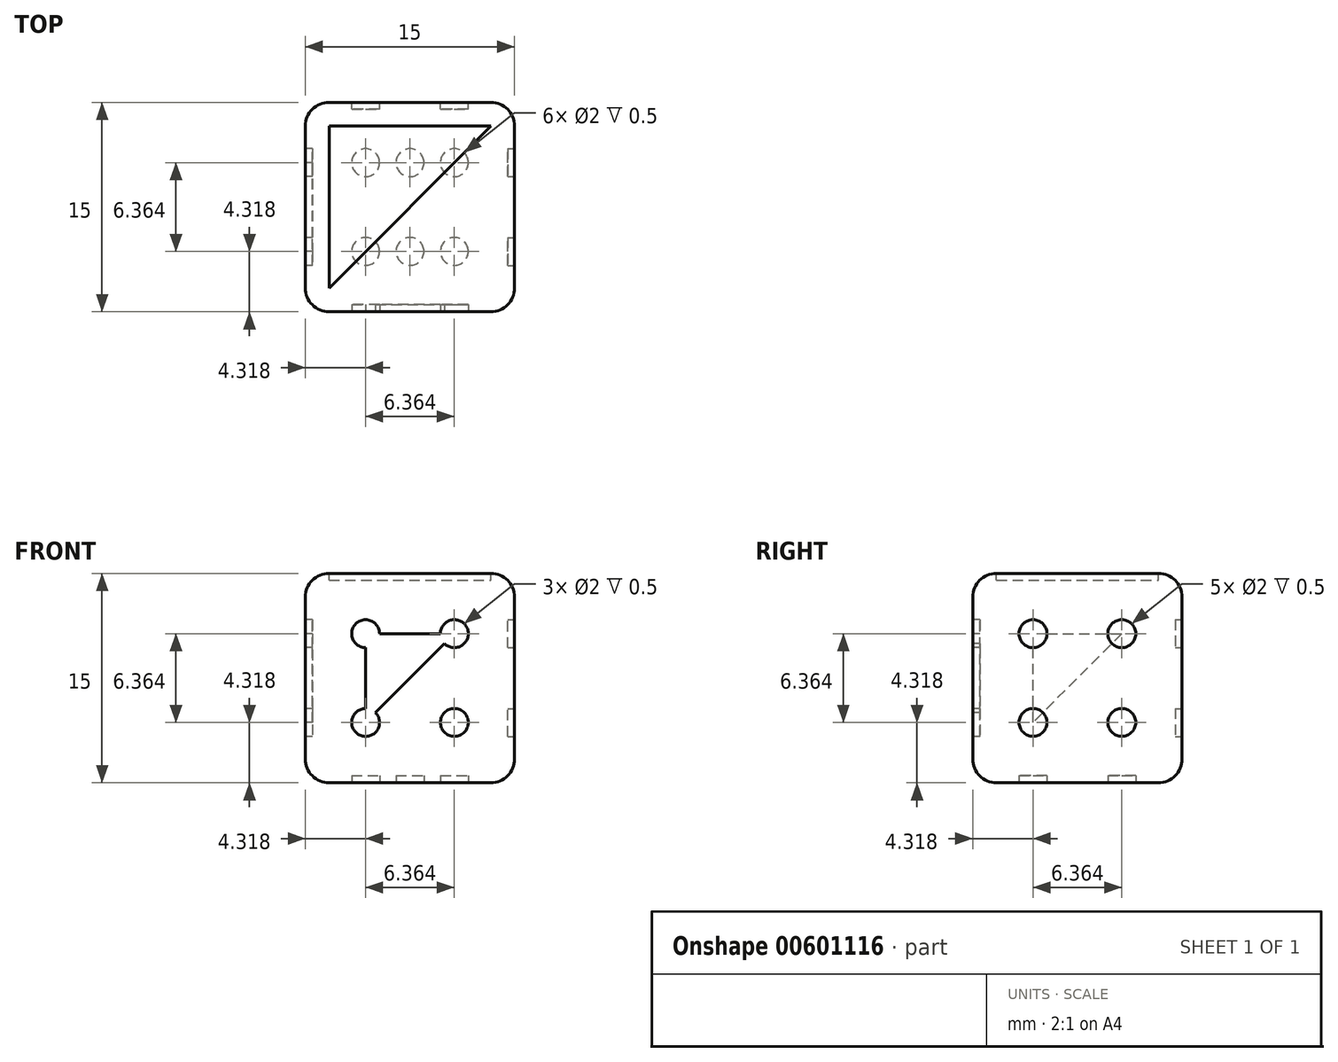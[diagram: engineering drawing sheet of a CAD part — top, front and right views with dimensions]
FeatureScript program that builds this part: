
annotation { "Feature Type Name" : "Feature", "Feature Type Description" : "" }
export const myFeature = defineFeature(function(context is Context, id is Id, definition is map)
    precondition{}
    {
        {
            var Q0;
            Q0=qCreatedBy(makeId("Front.planeOp"),FACE);
            var sketch = newSketch(context, id + "F0", { "sketchPlane" : qUnion([Q0])});
            skLineSegment(sketch, "E0.bottom", {"start": v(7.5, -7.5) * mm, "end": v(-7.5, -7.5) * mm});
            skLineSegment(sketch, "E0.top", {"start": v(7.5, 7.5) * mm, "end": v(-7.5, 7.5) * mm});
            skLineSegment(sketch, "E0.left", {"start": v(7.5, -7.5) * mm, "end": v(7.5, 7.5) * mm});
            skLineSegment(sketch, "E0.right", {"start": v(-7.5, -7.5) * mm, "end": v(-7.5, 7.5) * mm});
            skPoint(sketch, "E0.middle", {"position": v(0, 0) * mm});
            skSolve(sketch);
        }
        {
            var Q0;
            Q0 = qSketchRegion(id + "F0", true);
            extrude(context, id + "F1", {"entities" : qUnion([Q0]), "depth" : 15 * mm, "offsetDistance" : 25.4 * mm});
        }
        {
            var Q0;
            Q0=makeQuery(id+"F1.opExtrude","SWEPT_EDGE",EDGE,{"disambiguationData":[OSD([sQuery(id+"F0.wireOp",EDGE,"E0.bottom"),sQuery(id+"F0.wireOp",EDGE,"E0.right")])]});
            var Q1;
            Q1=makeQuery(id+"F1.opExtrude","CAP_EDGE",EDGE,{"disambiguationData":[OSD([sQuery(id+"F0.wireOp",EDGE,"E0.bottom")])],"isStart":true});
            var Q2;
            Q2=makeQuery(id+"F1.opExtrude","CAP_EDGE",EDGE,{"disambiguationData":[OSD([sQuery(id+"F0.wireOp",EDGE,"E0.right")])],"isStart":true});
            var Q3;
            Q3=makeQuery(id+"F1.opExtrude","CAP_EDGE",EDGE,{"disambiguationData":[OSD([sQuery(id+"F0.wireOp",EDGE,"E0.bottom")])],"isStart":false});
            var Q4;
            Q4=makeQuery(id+"F1.opExtrude","SWEPT_EDGE",EDGE,{"disambiguationData":[OSD([sQuery(id+"F0.wireOp",EDGE,"E0.bottom"),sQuery(id+"F0.wireOp",EDGE,"E0.left")])]});
            var Q5;
            Q5=makeQuery(id+"F1.opExtrude","CAP_EDGE",EDGE,{"disambiguationData":[OSD([sQuery(id+"F0.wireOp",EDGE,"E0.left")])],"isStart":false});
            var Q6;
            Q6=makeQuery(id+"F1.opExtrude","CAP_EDGE",EDGE,{"disambiguationData":[OSD([sQuery(id+"F0.wireOp",EDGE,"E0.right")])],"isStart":false});
            var Q7;
            Q7=makeQuery(id+"F1.opExtrude","SWEPT_FACE",FACE,{"disambiguationData":[OSD([sQuery(id+"F0.wireOp",EDGE,"E0.top")])]});
            var Q8;
            Q8=makeQuery(id+"F1.opExtrude","CAP_EDGE",EDGE,{"disambiguationData":[OSD([sQuery(id+"F0.wireOp",EDGE,"E0.left")])],"isStart":true});
            fillet(context, id + "F2", {"entities" : qUnion([Q0, Q1, Q2, Q3, Q4, Q5, Q6, Q7, Q8]), "radius" : 1.7 * mm, "tangentPropagation" : true, "allowEdgeOverflow" : false});
        }
        {
            var Q0;
            Q0=makeQuery(id+"F1.opExtrude","SWEPT_FACE",FACE,{"disambiguationData":[OSD([sQuery(id+"F0.wireOp",EDGE,"E0.top")])]});
            var sketch = newSketch(context, id + "F3", { "sketchPlane" : qUnion([Q0])});
            skLineSegment(sketch, "E1", {"start": v(5.8, -13.3) * mm, "end": v(-5.8, -1.7) * mm});
            skLineSegment(sketch, "E2", {"start": v(-5.8, -1.7) * mm, "end": v(-5.8, -13.3) * mm});
            skLineSegment(sketch, "E3", {"start": v(-5.8, -13.3) * mm, "end": v(5.8, -1.7) * mm});
            skCircle(sketch, "E4", {"center": v(0, -7.5) * mm, "radius": 1 * mm});
            skSolve(sketch);
        }
        {
            var Q0;
            Q0=makeQuery(id+"F1.opExtrude","SWEPT_FACE",FACE,{"disambiguationData":[OSD([sQuery(id+"F0.wireOp",EDGE,"E0.bottom")])]});
            var sketch = newSketch(context, id + "F4", { "sketchPlane" : qUnion([Q0])});
            skLineSegment(sketch, "E5", {"start": v(-5.8, 13.3) * mm, "end": v(-5.8, 1.7) * mm});
            skPoint(sketch, "E6.middle", {"position": v(0, 7.5) * mm});
            skCircle(sketch, "E7", {"center": v(-3.18, 4.32) * mm, "radius": 1 * mm});
            skCircle(sketch, "E8", {"center": v(0, 4.32) * mm, "radius": 1 * mm});
            skCircle(sketch, "E9", {"center": v(3.18, 4.32) * mm, "radius": 1 * mm});
            skCircle(sketch, "E10", {"center": v(3.18, 10.68) * mm, "radius": 1 * mm});
            skCircle(sketch, "E11", {"center": v(-3.18, 10.68) * mm, "radius": 1 * mm});
            skCircle(sketch, "E12", {"center": v(0, 10.68) * mm, "radius": 1 * mm});
            skSolve(sketch);
        }
        {
            var Q0;
            Q0=makeQuery(id+"F1.opExtrude","CAP_FACE",FACE,{"disambiguationData":[OSD([sQuery(id+"F0.wireOp",EDGE,"E0.bottom"),sQuery(id+"F0.wireOp",EDGE,"E0.top"),sQuery(id+"F0.wireOp",EDGE,"E0.left"),sQuery(id+"F0.wireOp",EDGE,"E0.right")])],"isStart":false});
            var sketch = newSketch(context, id + "F5", { "sketchPlane" : qUnion([Q0])});
            skLineSegment(sketch, "E13", {"start": v(5.8, -5.8) * mm, "end": v(-5.8, 5.8) * mm});
            skLineSegment(sketch, "E14", {"start": v(-5.8, 5.8) * mm, "end": v(-5.8, -5.8) * mm});
            skLineSegment(sketch, "E15", {"start": v(-5.8, -5.8) * mm, "end": v(5.8, 5.8) * mm});
            skLineSegment(sketch, "E16.bottom", {"start": v(3.18, 3.18) * mm, "end": v(-3.18, 3.18) * mm});
            skLineSegment(sketch, "E16.top", {"start": v(3.18, -3.18) * mm, "end": v(-3.18, -3.18) * mm});
            skLineSegment(sketch, "E16.left", {"start": v(3.18, 3.18) * mm, "end": v(3.18, -3.18) * mm});
            skLineSegment(sketch, "E16.right", {"start": v(-3.18, 3.18) * mm, "end": v(-3.18, -3.18) * mm});
            skPoint(sketch, "E16.middle", {"position": v(0, 0) * mm});
            skCircle(sketch, "E17", {"center": v(-3.18, -3.18) * mm, "radius": 1 * mm});
            skCircle(sketch, "E18", {"center": v(0, 0) * mm, "radius": 1 * mm});
            skCircle(sketch, "E19", {"center": v(-3.18, 3.18) * mm, "radius": 1 * mm});
            skCircle(sketch, "E20", {"center": v(3.18, 3.18) * mm, "radius": 1 * mm});
            skCircle(sketch, "E21", {"center": v(3.18, -3.18) * mm, "radius": 1 * mm});
            skSolve(sketch);
        }
        {
            var Q0;
            Q0=makeQuery(id+"F1.opExtrude","CAP_FACE",FACE,{"disambiguationData":[OSD([sQuery(id+"F0.wireOp",EDGE,"E0.bottom"),sQuery(id+"F0.wireOp",EDGE,"E0.top"),sQuery(id+"F0.wireOp",EDGE,"E0.left"),sQuery(id+"F0.wireOp",EDGE,"E0.right")])],"isStart":true});
            var sketch = newSketch(context, id + "F6", { "sketchPlane" : qUnion([Q0])});
            skLineSegment(sketch, "E22", {"start": v(-5.8, 5.8) * mm, "end": v(5.8, -5.8) * mm});
            skLineSegment(sketch, "E23", {"start": v(5.8, 5.8) * mm, "end": v(-5.8, -5.8) * mm});
            skLineSegment(sketch, "E24.bottom", {"start": v(-3.18, -3.18) * mm, "end": v(3.18, -3.18) * mm});
            skLineSegment(sketch, "E24.top", {"start": v(-3.18, 3.18) * mm, "end": v(3.18, 3.18) * mm});
            skLineSegment(sketch, "E24.left", {"start": v(-3.18, -3.18) * mm, "end": v(-3.18, 3.18) * mm});
            skLineSegment(sketch, "E24.right", {"start": v(3.18, -3.18) * mm, "end": v(3.18, 3.18) * mm});
            skPoint(sketch, "E24.middle", {"position": v(0, 0) * mm});
            skCircle(sketch, "E25", {"center": v(3.18, -3.18) * mm, "radius": 1 * mm});
            skCircle(sketch, "E26", {"center": v(-3.18, 3.18) * mm, "radius": 1 * mm});
            skSolve(sketch);
        }
        {
            var Q0;
            Q0=makeQuery(id+"F1.opExtrude","SWEPT_FACE",FACE,{"disambiguationData":[OSD([sQuery(id+"F0.wireOp",EDGE,"E0.right")])]});
            var sketch = newSketch(context, id + "F7", { "sketchPlane" : qUnion([Q0])});
            skLineSegment(sketch, "E27", {"start": v(1.7, -5.8) * mm, "end": v(13.3, 5.8) * mm});
            skLineSegment(sketch, "E28", {"start": v(13.3, 5.8) * mm, "end": v(1.7, 5.8) * mm});
            skLineSegment(sketch, "E29", {"start": v(1.7, 5.8) * mm, "end": v(13.3, -5.8) * mm});
            skLineSegment(sketch, "E30.bottom", {"start": v(10.68, -3.18) * mm, "end": v(4.32, -3.18) * mm});
            skLineSegment(sketch, "E30.top", {"start": v(10.68, 3.18) * mm, "end": v(4.32, 3.18) * mm});
            skLineSegment(sketch, "E30.left", {"start": v(10.68, -3.18) * mm, "end": v(10.68, 3.18) * mm});
            skLineSegment(sketch, "E30.right", {"start": v(4.32, -3.18) * mm, "end": v(4.32, 3.18) * mm});
            skPoint(sketch, "E30.middle", {"position": v(7.5, 0) * mm});
            skCircle(sketch, "E31", {"center": v(10.68, 3.18) * mm, "radius": 1 * mm});
            skCircle(sketch, "E32", {"center": v(7.5, 0) * mm, "radius": 1 * mm});
            skCircle(sketch, "E33", {"center": v(4.32, -3.18) * mm, "radius": 1 * mm});
            skSolve(sketch);
        }
        {
            var Q0;
            Q0=makeQuery(id+"F1.opExtrude","SWEPT_FACE",FACE,{"disambiguationData":[OSD([sQuery(id+"F0.wireOp",EDGE,"E0.left")])]});
            var sketch = newSketch(context, id + "F8", { "sketchPlane" : qUnion([Q0])});
            skLineSegment(sketch, "E34", {"start": v(-13.3, -5.8) * mm, "end": v(-1.7, 5.8) * mm});
            skLineSegment(sketch, "E35", {"start": v(-1.7, 5.8) * mm, "end": v(-1.7, -5.8) * mm});
            skLineSegment(sketch, "E36", {"start": v(-1.7, -5.8) * mm, "end": v(-13.3, 5.8) * mm});
            skLineSegment(sketch, "E37.bottom", {"start": v(-4.32, -3.18) * mm, "end": v(-10.68, -3.18) * mm});
            skLineSegment(sketch, "E37.top", {"start": v(-4.32, 3.18) * mm, "end": v(-10.68, 3.18) * mm});
            skLineSegment(sketch, "E37.left", {"start": v(-4.32, -3.18) * mm, "end": v(-4.32, 3.18) * mm});
            skLineSegment(sketch, "E37.right", {"start": v(-10.68, -3.18) * mm, "end": v(-10.68, 3.18) * mm});
            skPoint(sketch, "E37.middle", {"position": v(-7.5, 0) * mm});
            skCircle(sketch, "E38", {"center": v(-10.68, 3.18) * mm, "radius": 1 * mm});
            skCircle(sketch, "E39", {"center": v(-4.32, 3.18) * mm, "radius": 1 * mm});
            skCircle(sketch, "E40", {"center": v(-4.32, -3.18) * mm, "radius": 1 * mm});
            skCircle(sketch, "E41", {"center": v(-10.68, -3.18) * mm, "radius": 1 * mm});
            skSolve(sketch);
        }
        {
            var Q0;
            Q0 = qSketchRegion(id + "F4", true);
            extrude(context, id + "F9", {"entities" : qUnion([Q0]), "operationType" : NewBodyOperationType.REMOVE, "oppositeDirection" : true, "depth" : 0.5 * mm, "offsetDistance" : 25 * mm});
        }
        {
            var Q0;
            {var subQ1=sQuery(id+"F5.wireOp",EDGE,"E15");var subQ3=sQuery(id+"F5.wireOp",EDGE,"E17");var subQ4=makeQuery(id+"F5.imprint","INTERSECT",VERTEX,{"disambiguationData":[OD(0.0)],"derivedFrom":[subQ1,subQ3]});Q0=makeQuery(id+"F5.imprint","IMPRINT",FACE,{"disambiguationData":[TD([[makeQuery(id+"F5.imprint","IMPRINT",EDGE,{"disambiguationData":[TD([[subQ4,-1.0]])],"derivedFrom":subQ3}),1.0]])]});}
            var Q1;
            {var subQ1=sQuery(id+"F5.wireOp",EDGE,"E15");var subQ3=sQuery(id+"F5.wireOp",EDGE,"E17");var subQ4=makeQuery(id+"F5.imprint","INTERSECT",VERTEX,{"disambiguationData":[OD(0.0)],"derivedFrom":[subQ1,subQ3]});Q1=makeQuery(id+"F5.imprint","IMPRINT",FACE,{"disambiguationData":[TD([[makeQuery(id+"F5.imprint","IMPRINT",EDGE,{"disambiguationData":[TD([[subQ4,1.0]])],"derivedFrom":subQ3}),1.0]])]});}
            var Q2;
            {var subQ1=sQuery(id+"F5.wireOp",EDGE,"E15");var subQ3=sQuery(id+"F5.wireOp",EDGE,"E17");var subQ4=makeQuery(id+"F5.imprint","INTERSECT",VERTEX,{"disambiguationData":[OD(1.0)],"derivedFrom":[subQ1,subQ3]});Q2=makeQuery(id+"F5.imprint","IMPRINT",FACE,{"disambiguationData":[TD([[makeQuery(id+"F5.imprint","IMPRINT",EDGE,{"disambiguationData":[TD([[subQ4,-1.0]])],"derivedFrom":subQ3}),1.0]])]});}
            var Q3;
            {var subQ1=sQuery(id+"F5.wireOp",EDGE,"E15");var subQ3=sQuery(id+"F5.wireOp",EDGE,"E17");var subQ4=makeQuery(id+"F5.imprint","INTERSECT",VERTEX,{"disambiguationData":[OD(1.0)],"derivedFrom":[subQ1,subQ3]});Q3=makeQuery(id+"F5.imprint","IMPRINT",FACE,{"disambiguationData":[TD([[makeQuery(id+"F5.imprint","IMPRINT",EDGE,{"disambiguationData":[TD([[subQ4,1.0]])],"derivedFrom":subQ3}),1.0]])]});}
            var Q4;
            {var subQ1=sQuery(id+"F5.wireOp",EDGE,"E13");var subQ3=sQuery(id+"F5.wireOp",EDGE,"E19");var subQ4=makeQuery(id+"F5.imprint","INTERSECT",VERTEX,{"disambiguationData":[OD(0.0)],"derivedFrom":[subQ1,subQ3]});Q4=makeQuery(id+"F5.imprint","IMPRINT",FACE,{"disambiguationData":[TD([[makeQuery(id+"F5.imprint","IMPRINT",EDGE,{"disambiguationData":[TD([[subQ4,1.0]])],"derivedFrom":subQ3}),1.0]])]});}
            var Q5;
            {var subQ1=sQuery(id+"F5.wireOp",EDGE,"E13");var subQ3=sQuery(id+"F5.wireOp",EDGE,"E19");var subQ4=makeQuery(id+"F5.imprint","INTERSECT",VERTEX,{"disambiguationData":[OD(1.0)],"derivedFrom":[subQ1,subQ3]});Q5=makeQuery(id+"F5.imprint","IMPRINT",FACE,{"disambiguationData":[TD([[makeQuery(id+"F5.imprint","IMPRINT",EDGE,{"disambiguationData":[TD([[subQ4,1.0]])],"derivedFrom":subQ3}),1.0]])]});}
            var Q6;
            {var subQ1=sQuery(id+"F5.wireOp",EDGE,"E13");var subQ3=sQuery(id+"F5.wireOp",EDGE,"E19");var subQ4=makeQuery(id+"F5.imprint","INTERSECT",VERTEX,{"disambiguationData":[OD(1.0)],"derivedFrom":[subQ1,subQ3]});Q6=makeQuery(id+"F5.imprint","IMPRINT",FACE,{"disambiguationData":[TD([[makeQuery(id+"F5.imprint","IMPRINT",EDGE,{"disambiguationData":[TD([[subQ4,-1.0]])],"derivedFrom":subQ3}),1.0]])]});}
            var Q7;
            {var subQ1=sQuery(id+"F5.wireOp",EDGE,"E13");var subQ3=sQuery(id+"F5.wireOp",EDGE,"E19");var subQ4=makeQuery(id+"F5.imprint","INTERSECT",VERTEX,{"disambiguationData":[OD(0.0)],"derivedFrom":[subQ1,subQ3]});Q7=makeQuery(id+"F5.imprint","IMPRINT",FACE,{"disambiguationData":[TD([[makeQuery(id+"F5.imprint","IMPRINT",EDGE,{"disambiguationData":[TD([[subQ4,-1.0]])],"derivedFrom":subQ3}),1.0]])]});}
            var Q8;
            {var subQ1=sQuery(id+"F5.wireOp",EDGE,"E15");var subQ3=sQuery(id+"F5.wireOp",EDGE,"E20");var subQ4=makeQuery(id+"F5.imprint","INTERSECT",VERTEX,{"disambiguationData":[OD(1.0)],"derivedFrom":[subQ1,subQ3]});Q8=makeQuery(id+"F5.imprint","IMPRINT",FACE,{"disambiguationData":[TD([[makeQuery(id+"F5.imprint","IMPRINT",EDGE,{"disambiguationData":[TD([[subQ4,-1.0]])],"derivedFrom":subQ3}),1.0]])]});}
            var Q9;
            {var subQ1=sQuery(id+"F5.wireOp",EDGE,"E15");var subQ3=sQuery(id+"F5.wireOp",EDGE,"E20");var subQ4=makeQuery(id+"F5.imprint","INTERSECT",VERTEX,{"disambiguationData":[OD(1.0)],"derivedFrom":[subQ1,subQ3]});Q9=makeQuery(id+"F5.imprint","IMPRINT",FACE,{"disambiguationData":[TD([[makeQuery(id+"F5.imprint","IMPRINT",EDGE,{"disambiguationData":[TD([[subQ4,1.0]])],"derivedFrom":subQ3}),1.0]])]});}
            var Q10;
            {var subQ1=sQuery(id+"F5.wireOp",EDGE,"E15");var subQ3=sQuery(id+"F5.wireOp",EDGE,"E20");var subQ4=makeQuery(id+"F5.imprint","INTERSECT",VERTEX,{"disambiguationData":[OD(0.0)],"derivedFrom":[subQ1,subQ3]});Q10=makeQuery(id+"F5.imprint","IMPRINT",FACE,{"disambiguationData":[TD([[makeQuery(id+"F5.imprint","IMPRINT",EDGE,{"disambiguationData":[TD([[subQ4,-1.0]])],"derivedFrom":subQ3}),1.0]])]});}
            var Q11;
            {var subQ1=sQuery(id+"F5.wireOp",EDGE,"E15");var subQ3=sQuery(id+"F5.wireOp",EDGE,"E20");var subQ4=makeQuery(id+"F5.imprint","INTERSECT",VERTEX,{"disambiguationData":[OD(0.0)],"derivedFrom":[subQ1,subQ3]});Q11=makeQuery(id+"F5.imprint","IMPRINT",FACE,{"disambiguationData":[TD([[makeQuery(id+"F5.imprint","IMPRINT",EDGE,{"disambiguationData":[TD([[subQ4,1.0]])],"derivedFrom":subQ3}),1.0]])]});}
            var Q12;
            {var subQ0=sQuery(id+"F5.wireOp",EDGE,"E15");var subQ1=sQuery(id+"F5.wireOp",EDGE,"E13");var subQ2=makeQuery(id+"F5.imprint","INTERSECT",VERTEX,{"derivedFrom":[subQ1,subQ0]});Q12=makeQuery(id+"F5.imprint","IMPRINT",FACE,{"disambiguationData":[TD([[makeQuery(id+"F5.imprint","IMPRINT",EDGE,{"disambiguationData":[TD([[subQ2,-1.0]])],"derivedFrom":subQ1}),1.0]])]});}
            var Q13;
            {var subQ0=sQuery(id+"F5.wireOp",EDGE,"E18");var subQ1=sQuery(id+"F5.wireOp",EDGE,"E13");var subQ2=makeQuery(id+"F5.imprint","INTERSECT",VERTEX,{"disambiguationData":[OD(0.0)],"derivedFrom":[subQ1,subQ0]});Q13=makeQuery(id+"F5.imprint","IMPRINT",FACE,{"disambiguationData":[TD([[makeQuery(id+"F5.imprint","IMPRINT",EDGE,{"disambiguationData":[TD([[subQ2,-1.0]])],"derivedFrom":subQ1}),1.0]])]});}
            var Q14;
            {var subQ0=sQuery(id+"F5.wireOp",EDGE,"E18");var subQ1=sQuery(id+"F5.wireOp",EDGE,"E13");var subQ2=makeQuery(id+"F5.imprint","INTERSECT",VERTEX,{"disambiguationData":[OD(0.0)],"derivedFrom":[subQ1,subQ0]});Q14=makeQuery(id+"F5.imprint","IMPRINT",FACE,{"disambiguationData":[TD([[makeQuery(id+"F5.imprint","IMPRINT",EDGE,{"disambiguationData":[TD([[subQ2,-1.0]])],"derivedFrom":subQ1}),-1.0]])]});}
            var Q15;
            {var subQ0=sQuery(id+"F5.wireOp",EDGE,"E15");var subQ1=sQuery(id+"F5.wireOp",EDGE,"E13");var subQ2=makeQuery(id+"F5.imprint","INTERSECT",VERTEX,{"derivedFrom":[subQ1,subQ0]});Q15=makeQuery(id+"F5.imprint","IMPRINT",FACE,{"disambiguationData":[TD([[makeQuery(id+"F5.imprint","IMPRINT",EDGE,{"disambiguationData":[TD([[subQ2,-1.0]])],"derivedFrom":subQ1}),-1.0]])]});}
            var Q16;
            {var subQ1=sQuery(id+"F5.wireOp",EDGE,"E13");var subQ3=sQuery(id+"F5.wireOp",EDGE,"E21");var subQ4=makeQuery(id+"F5.imprint","INTERSECT",VERTEX,{"disambiguationData":[OD(1.0)],"derivedFrom":[subQ1,subQ3]});Q16=makeQuery(id+"F5.imprint","IMPRINT",FACE,{"disambiguationData":[TD([[makeQuery(id+"F5.imprint","IMPRINT",EDGE,{"disambiguationData":[TD([[subQ4,1.0]])],"derivedFrom":subQ3}),1.0]])]});}
            var Q17;
            {var subQ1=sQuery(id+"F5.wireOp",EDGE,"E13");var subQ3=sQuery(id+"F5.wireOp",EDGE,"E21");var subQ4=makeQuery(id+"F5.imprint","INTERSECT",VERTEX,{"disambiguationData":[OD(0.0)],"derivedFrom":[subQ1,subQ3]});Q17=makeQuery(id+"F5.imprint","IMPRINT",FACE,{"disambiguationData":[TD([[makeQuery(id+"F5.imprint","IMPRINT",EDGE,{"disambiguationData":[TD([[subQ4,-1.0]])],"derivedFrom":subQ3}),1.0]])]});}
            var Q18;
            {var subQ1=sQuery(id+"F5.wireOp",EDGE,"E13");var subQ3=sQuery(id+"F5.wireOp",EDGE,"E21");var subQ4=makeQuery(id+"F5.imprint","INTERSECT",VERTEX,{"disambiguationData":[OD(0.0)],"derivedFrom":[subQ1,subQ3]});Q18=makeQuery(id+"F5.imprint","IMPRINT",FACE,{"disambiguationData":[TD([[makeQuery(id+"F5.imprint","IMPRINT",EDGE,{"disambiguationData":[TD([[subQ4,1.0]])],"derivedFrom":subQ3}),1.0]])]});}
            var Q19;
            {var subQ1=sQuery(id+"F5.wireOp",EDGE,"E13");var subQ3=sQuery(id+"F5.wireOp",EDGE,"E21");var subQ4=makeQuery(id+"F5.imprint","INTERSECT",VERTEX,{"disambiguationData":[OD(1.0)],"derivedFrom":[subQ1,subQ3]});Q19=makeQuery(id+"F5.imprint","IMPRINT",FACE,{"disambiguationData":[TD([[makeQuery(id+"F5.imprint","IMPRINT",EDGE,{"disambiguationData":[TD([[subQ4,-1.0]])],"derivedFrom":subQ3}),1.0]])]});}
            extrude(context, id + "F10", {"entities" : qUnion([Q0, Q1, Q2, Q3, Q4, Q5, Q6, Q7, Q8, Q9, Q10, Q11, Q12, Q13, Q14, Q15, Q16, Q17, Q18, Q19]), "operationType" : NewBodyOperationType.REMOVE, "oppositeDirection" : true, "depth" : 0.5 * mm, "offsetDistance" : 25 * mm});
        }
        {
            var Q0;
            {var subQ1=sQuery(id+"F8.wireOp",EDGE,"E34");var subQ3=sQuery(id+"F8.wireOp",EDGE,"E41");var subQ4=makeQuery(id+"F8.imprint","INTERSECT",VERTEX,{"disambiguationData":[OD(0.0)],"derivedFrom":[subQ1,subQ3]});Q0=makeQuery(id+"F8.imprint","IMPRINT",FACE,{"disambiguationData":[TD([[makeQuery(id+"F8.imprint","IMPRINT",EDGE,{"disambiguationData":[TD([[subQ4,1.0]])],"derivedFrom":subQ3}),1.0]])]});}
            var Q1;
            {var subQ1=sQuery(id+"F8.wireOp",EDGE,"E34");var subQ3=sQuery(id+"F8.wireOp",EDGE,"E41");var subQ4=makeQuery(id+"F8.imprint","INTERSECT",VERTEX,{"disambiguationData":[OD(0.0)],"derivedFrom":[subQ1,subQ3]});Q1=makeQuery(id+"F8.imprint","IMPRINT",FACE,{"disambiguationData":[TD([[makeQuery(id+"F8.imprint","IMPRINT",EDGE,{"disambiguationData":[TD([[subQ4,-1.0]])],"derivedFrom":subQ3}),1.0]])]});}
            var Q2;
            {var subQ1=sQuery(id+"F8.wireOp",EDGE,"E34");var subQ3=sQuery(id+"F8.wireOp",EDGE,"E41");var subQ4=makeQuery(id+"F8.imprint","INTERSECT",VERTEX,{"disambiguationData":[OD(1.0)],"derivedFrom":[subQ1,subQ3]});Q2=makeQuery(id+"F8.imprint","IMPRINT",FACE,{"disambiguationData":[TD([[makeQuery(id+"F8.imprint","IMPRINT",EDGE,{"disambiguationData":[TD([[subQ4,1.0]])],"derivedFrom":subQ3}),1.0]])]});}
            var Q3;
            {var subQ1=sQuery(id+"F8.wireOp",EDGE,"E34");var subQ3=sQuery(id+"F8.wireOp",EDGE,"E41");var subQ4=makeQuery(id+"F8.imprint","INTERSECT",VERTEX,{"disambiguationData":[OD(1.0)],"derivedFrom":[subQ1,subQ3]});Q3=makeQuery(id+"F8.imprint","IMPRINT",FACE,{"disambiguationData":[TD([[makeQuery(id+"F8.imprint","IMPRINT",EDGE,{"disambiguationData":[TD([[subQ4,-1.0]])],"derivedFrom":subQ3}),1.0]])]});}
            var Q4;
            {var subQ1=sQuery(id+"F8.wireOp",EDGE,"E36");var subQ3=sQuery(id+"F8.wireOp",EDGE,"E38");var subQ4=makeQuery(id+"F8.imprint","INTERSECT",VERTEX,{"disambiguationData":[OD(0.0)],"derivedFrom":[subQ1,subQ3]});Q4=makeQuery(id+"F8.imprint","IMPRINT",FACE,{"disambiguationData":[TD([[makeQuery(id+"F8.imprint","IMPRINT",EDGE,{"disambiguationData":[TD([[subQ4,1.0]])],"derivedFrom":subQ3}),1.0]])]});}
            var Q5;
            {var subQ1=sQuery(id+"F8.wireOp",EDGE,"E36");var subQ3=sQuery(id+"F8.wireOp",EDGE,"E38");var subQ4=makeQuery(id+"F8.imprint","INTERSECT",VERTEX,{"disambiguationData":[OD(0.0)],"derivedFrom":[subQ1,subQ3]});Q5=makeQuery(id+"F8.imprint","IMPRINT",FACE,{"disambiguationData":[TD([[makeQuery(id+"F8.imprint","IMPRINT",EDGE,{"disambiguationData":[TD([[subQ4,-1.0]])],"derivedFrom":subQ3}),1.0]])]});}
            var Q6;
            {var subQ1=sQuery(id+"F8.wireOp",EDGE,"E36");var subQ3=sQuery(id+"F8.wireOp",EDGE,"E38");var subQ4=makeQuery(id+"F8.imprint","INTERSECT",VERTEX,{"disambiguationData":[OD(1.0)],"derivedFrom":[subQ1,subQ3]});Q6=makeQuery(id+"F8.imprint","IMPRINT",FACE,{"disambiguationData":[TD([[makeQuery(id+"F8.imprint","IMPRINT",EDGE,{"disambiguationData":[TD([[subQ4,1.0]])],"derivedFrom":subQ3}),1.0]])]});}
            var Q7;
            {var subQ1=sQuery(id+"F8.wireOp",EDGE,"E36");var subQ3=sQuery(id+"F8.wireOp",EDGE,"E38");var subQ4=makeQuery(id+"F8.imprint","INTERSECT",VERTEX,{"disambiguationData":[OD(1.0)],"derivedFrom":[subQ1,subQ3]});Q7=makeQuery(id+"F8.imprint","IMPRINT",FACE,{"disambiguationData":[TD([[makeQuery(id+"F8.imprint","IMPRINT",EDGE,{"disambiguationData":[TD([[subQ4,-1.0]])],"derivedFrom":subQ3}),1.0]])]});}
            var Q8;
            {var subQ1=sQuery(id+"F8.wireOp",EDGE,"E34");var subQ3=sQuery(id+"F8.wireOp",EDGE,"E39");var subQ4=makeQuery(id+"F8.imprint","INTERSECT",VERTEX,{"disambiguationData":[OD(1.0)],"derivedFrom":[subQ1,subQ3]});Q8=makeQuery(id+"F8.imprint","IMPRINT",FACE,{"disambiguationData":[TD([[makeQuery(id+"F8.imprint","IMPRINT",EDGE,{"disambiguationData":[TD([[subQ4,1.0]])],"derivedFrom":subQ3}),1.0]])]});}
            var Q9;
            {var subQ1=sQuery(id+"F8.wireOp",EDGE,"E36");var subQ3=sQuery(id+"F8.wireOp",EDGE,"E40");var subQ4=makeQuery(id+"F8.imprint","INTERSECT",VERTEX,{"disambiguationData":[OD(0.0)],"derivedFrom":[subQ1,subQ3]});Q9=makeQuery(id+"F8.imprint","IMPRINT",FACE,{"disambiguationData":[TD([[makeQuery(id+"F8.imprint","IMPRINT",EDGE,{"disambiguationData":[TD([[subQ4,1.0]])],"derivedFrom":subQ3}),1.0]])]});}
            var Q10;
            {var subQ1=sQuery(id+"F8.wireOp",EDGE,"E36");var subQ3=sQuery(id+"F8.wireOp",EDGE,"E40");var subQ4=makeQuery(id+"F8.imprint","INTERSECT",VERTEX,{"disambiguationData":[OD(0.0)],"derivedFrom":[subQ1,subQ3]});Q10=makeQuery(id+"F8.imprint","IMPRINT",FACE,{"disambiguationData":[TD([[makeQuery(id+"F8.imprint","IMPRINT",EDGE,{"disambiguationData":[TD([[subQ4,-1.0]])],"derivedFrom":subQ3}),1.0]])]});}
            var Q11;
            {var subQ1=sQuery(id+"F8.wireOp",EDGE,"E36");var subQ3=sQuery(id+"F8.wireOp",EDGE,"E40");var subQ4=makeQuery(id+"F8.imprint","INTERSECT",VERTEX,{"disambiguationData":[OD(1.0)],"derivedFrom":[subQ1,subQ3]});Q11=makeQuery(id+"F8.imprint","IMPRINT",FACE,{"disambiguationData":[TD([[makeQuery(id+"F8.imprint","IMPRINT",EDGE,{"disambiguationData":[TD([[subQ4,1.0]])],"derivedFrom":subQ3}),1.0]])]});}
            var Q12;
            {var subQ1=sQuery(id+"F8.wireOp",EDGE,"E36");var subQ3=sQuery(id+"F8.wireOp",EDGE,"E40");var subQ4=makeQuery(id+"F8.imprint","INTERSECT",VERTEX,{"disambiguationData":[OD(1.0)],"derivedFrom":[subQ1,subQ3]});Q12=makeQuery(id+"F8.imprint","IMPRINT",FACE,{"disambiguationData":[TD([[makeQuery(id+"F8.imprint","IMPRINT",EDGE,{"disambiguationData":[TD([[subQ4,-1.0]])],"derivedFrom":subQ3}),1.0]])]});}
            var Q13;
            {var subQ1=sQuery(id+"F8.wireOp",EDGE,"E34");var subQ3=sQuery(id+"F8.wireOp",EDGE,"E39");var subQ4=makeQuery(id+"F8.imprint","INTERSECT",VERTEX,{"disambiguationData":[OD(0.0)],"derivedFrom":[subQ1,subQ3]});Q13=makeQuery(id+"F8.imprint","IMPRINT",FACE,{"disambiguationData":[TD([[makeQuery(id+"F8.imprint","IMPRINT",EDGE,{"disambiguationData":[TD([[subQ4,-1.0]])],"derivedFrom":subQ3}),1.0]])]});}
            var Q14;
            {var subQ1=sQuery(id+"F8.wireOp",EDGE,"E34");var subQ3=sQuery(id+"F8.wireOp",EDGE,"E39");var subQ4=makeQuery(id+"F8.imprint","INTERSECT",VERTEX,{"disambiguationData":[OD(0.0)],"derivedFrom":[subQ1,subQ3]});Q14=makeQuery(id+"F8.imprint","IMPRINT",FACE,{"disambiguationData":[TD([[makeQuery(id+"F8.imprint","IMPRINT",EDGE,{"disambiguationData":[TD([[subQ4,1.0]])],"derivedFrom":subQ3}),1.0]])]});}
            var Q15;
            {var subQ1=sQuery(id+"F8.wireOp",EDGE,"E34");var subQ3=sQuery(id+"F8.wireOp",EDGE,"E39");var subQ4=makeQuery(id+"F8.imprint","INTERSECT",VERTEX,{"disambiguationData":[OD(1.0)],"derivedFrom":[subQ1,subQ3]});Q15=makeQuery(id+"F8.imprint","IMPRINT",FACE,{"disambiguationData":[TD([[makeQuery(id+"F8.imprint","IMPRINT",EDGE,{"disambiguationData":[TD([[subQ4,-1.0]])],"derivedFrom":subQ3}),1.0]])]});}
            extrude(context, id + "F11", {"entities" : qUnion([Q0, Q1, Q2, Q3, Q4, Q5, Q6, Q7, Q8, Q9, Q10, Q11, Q12, Q13, Q14, Q15]), "operationType" : NewBodyOperationType.REMOVE, "oppositeDirection" : true, "depth" : 0.5 * mm, "offsetDistance" : 25 * mm});
        }
        {
            var Q0;
            {var subQ0=sQuery(id+"F3.wireOp",EDGE,"E4");var subQ1=sQuery(id+"F3.wireOp",EDGE,"E1");var subQ2=makeQuery(id+"F3.imprint","INTERSECT",VERTEX,{"disambiguationData":[OD(0.0)],"derivedFrom":[subQ1,subQ0]});Q0=makeQuery(id+"F3.imprint","IMPRINT",FACE,{"disambiguationData":[TD([[makeQuery(id+"F3.imprint","IMPRINT",EDGE,{"disambiguationData":[TD([[subQ2,-1.0]])],"derivedFrom":subQ1}),1.0]])]});}
            var Q1;
            {var subQ0=sQuery(id+"F3.wireOp",EDGE,"E4");var subQ1=sQuery(id+"F3.wireOp",EDGE,"E1");var subQ2=makeQuery(id+"F3.imprint","INTERSECT",VERTEX,{"disambiguationData":[OD(0.0)],"derivedFrom":[subQ1,subQ0]});Q1=makeQuery(id+"F3.imprint","IMPRINT",FACE,{"disambiguationData":[TD([[makeQuery(id+"F3.imprint","IMPRINT",EDGE,{"disambiguationData":[TD([[subQ2,-1.0]])],"derivedFrom":subQ1}),-1.0]])]});}
            var Q2;
            {var subQ0=sQuery(id+"F3.wireOp",EDGE,"E3");var subQ1=sQuery(id+"F3.wireOp",EDGE,"E1");var subQ2=makeQuery(id+"F3.imprint","INTERSECT",VERTEX,{"derivedFrom":[subQ1,subQ0]});Q2=makeQuery(id+"F3.imprint","IMPRINT",FACE,{"disambiguationData":[TD([[makeQuery(id+"F3.imprint","IMPRINT",EDGE,{"disambiguationData":[TD([[subQ2,-1.0]])],"derivedFrom":subQ1}),-1.0]])]});}
            var Q3;
            {var subQ0=sQuery(id+"F3.wireOp",EDGE,"E3");var subQ1=sQuery(id+"F3.wireOp",EDGE,"E1");var subQ2=makeQuery(id+"F3.imprint","INTERSECT",VERTEX,{"derivedFrom":[subQ1,subQ0]});Q3=makeQuery(id+"F3.imprint","IMPRINT",FACE,{"disambiguationData":[TD([[makeQuery(id+"F3.imprint","IMPRINT",EDGE,{"disambiguationData":[TD([[subQ2,-1.0]])],"derivedFrom":subQ1}),1.0]])]});}
            extrude(context, id + "F12", {"entities" : qUnion([Q0, Q1, Q2, Q3]), "operationType" : NewBodyOperationType.REMOVE, "oppositeDirection" : true, "depth" : 0.5 * mm, "offsetDistance" : 25 * mm});
        }
        {
            var Q0;
            {var subQ1=sQuery(id+"F7.wireOp",EDGE,"E27");var subQ3=sQuery(id+"F7.wireOp",EDGE,"E33");var subQ4=makeQuery(id+"F7.imprint","INTERSECT",VERTEX,{"disambiguationData":[OD(0.0)],"derivedFrom":[subQ1,subQ3]});Q0=makeQuery(id+"F7.imprint","IMPRINT",FACE,{"disambiguationData":[TD([[makeQuery(id+"F7.imprint","IMPRINT",EDGE,{"disambiguationData":[TD([[subQ4,-1.0]])],"derivedFrom":subQ3}),1.0]])]});}
            var Q1;
            {var subQ1=sQuery(id+"F7.wireOp",EDGE,"E27");var subQ3=sQuery(id+"F7.wireOp",EDGE,"E33");var subQ4=makeQuery(id+"F7.imprint","INTERSECT",VERTEX,{"disambiguationData":[OD(0.0)],"derivedFrom":[subQ1,subQ3]});Q1=makeQuery(id+"F7.imprint","IMPRINT",FACE,{"disambiguationData":[TD([[makeQuery(id+"F7.imprint","IMPRINT",EDGE,{"disambiguationData":[TD([[subQ4,1.0]])],"derivedFrom":subQ3}),1.0]])]});}
            var Q2;
            {var subQ1=sQuery(id+"F7.wireOp",EDGE,"E27");var subQ3=sQuery(id+"F7.wireOp",EDGE,"E33");var subQ4=makeQuery(id+"F7.imprint","INTERSECT",VERTEX,{"disambiguationData":[OD(1.0)],"derivedFrom":[subQ1,subQ3]});Q2=makeQuery(id+"F7.imprint","IMPRINT",FACE,{"disambiguationData":[TD([[makeQuery(id+"F7.imprint","IMPRINT",EDGE,{"disambiguationData":[TD([[subQ4,-1.0]])],"derivedFrom":subQ3}),1.0]])]});}
            var Q3;
            {var subQ1=sQuery(id+"F7.wireOp",EDGE,"E27");var subQ3=sQuery(id+"F7.wireOp",EDGE,"E33");var subQ4=makeQuery(id+"F7.imprint","INTERSECT",VERTEX,{"disambiguationData":[OD(1.0)],"derivedFrom":[subQ1,subQ3]});Q3=makeQuery(id+"F7.imprint","IMPRINT",FACE,{"disambiguationData":[TD([[makeQuery(id+"F7.imprint","IMPRINT",EDGE,{"disambiguationData":[TD([[subQ4,1.0]])],"derivedFrom":subQ3}),1.0]])]});}
            var Q4;
            {var subQ0=sQuery(id+"F7.wireOp",EDGE,"E32");var subQ1=sQuery(id+"F7.wireOp",EDGE,"E27");var subQ2=makeQuery(id+"F7.imprint","INTERSECT",VERTEX,{"disambiguationData":[OD(0.0)],"derivedFrom":[subQ1,subQ0]});Q4=makeQuery(id+"F7.imprint","IMPRINT",FACE,{"disambiguationData":[TD([[makeQuery(id+"F7.imprint","IMPRINT",EDGE,{"disambiguationData":[TD([[subQ2,-1.0]])],"derivedFrom":subQ1}),-1.0]])]});}
            var Q5;
            {var subQ0=sQuery(id+"F7.wireOp",EDGE,"E32");var subQ1=sQuery(id+"F7.wireOp",EDGE,"E27");var subQ2=makeQuery(id+"F7.imprint","INTERSECT",VERTEX,{"disambiguationData":[OD(0.0)],"derivedFrom":[subQ1,subQ0]});Q5=makeQuery(id+"F7.imprint","IMPRINT",FACE,{"disambiguationData":[TD([[makeQuery(id+"F7.imprint","IMPRINT",EDGE,{"disambiguationData":[TD([[subQ2,-1.0]])],"derivedFrom":subQ1}),1.0]])]});}
            var Q6;
            {var subQ0=sQuery(id+"F7.wireOp",EDGE,"E29");var subQ1=sQuery(id+"F7.wireOp",EDGE,"E27");var subQ2=makeQuery(id+"F7.imprint","INTERSECT",VERTEX,{"derivedFrom":[subQ1,subQ0]});Q6=makeQuery(id+"F7.imprint","IMPRINT",FACE,{"disambiguationData":[TD([[makeQuery(id+"F7.imprint","IMPRINT",EDGE,{"disambiguationData":[TD([[subQ2,-1.0]])],"derivedFrom":subQ1}),1.0]])]});}
            var Q7;
            {var subQ0=sQuery(id+"F7.wireOp",EDGE,"E29");var subQ1=sQuery(id+"F7.wireOp",EDGE,"E27");var subQ2=makeQuery(id+"F7.imprint","INTERSECT",VERTEX,{"derivedFrom":[subQ1,subQ0]});Q7=makeQuery(id+"F7.imprint","IMPRINT",FACE,{"disambiguationData":[TD([[makeQuery(id+"F7.imprint","IMPRINT",EDGE,{"disambiguationData":[TD([[subQ2,-1.0]])],"derivedFrom":subQ1}),-1.0]])]});}
            var Q8;
            {var subQ1=sQuery(id+"F7.wireOp",EDGE,"E27");var subQ3=sQuery(id+"F7.wireOp",EDGE,"E31");var subQ4=makeQuery(id+"F7.imprint","INTERSECT",VERTEX,{"disambiguationData":[OD(0.0)],"derivedFrom":[subQ1,subQ3]});Q8=makeQuery(id+"F7.imprint","IMPRINT",FACE,{"disambiguationData":[TD([[makeQuery(id+"F7.imprint","IMPRINT",EDGE,{"disambiguationData":[TD([[subQ4,1.0]])],"derivedFrom":subQ3}),1.0]])]});}
            var Q9;
            {var subQ1=sQuery(id+"F7.wireOp",EDGE,"E27");var subQ3=sQuery(id+"F7.wireOp",EDGE,"E31");var subQ4=makeQuery(id+"F7.imprint","INTERSECT",VERTEX,{"disambiguationData":[OD(0.0)],"derivedFrom":[subQ1,subQ3]});Q9=makeQuery(id+"F7.imprint","IMPRINT",FACE,{"disambiguationData":[TD([[makeQuery(id+"F7.imprint","IMPRINT",EDGE,{"disambiguationData":[TD([[subQ4,-1.0]])],"derivedFrom":subQ3}),1.0]])]});}
            var Q10;
            {var subQ1=sQuery(id+"F7.wireOp",EDGE,"E27");var subQ3=sQuery(id+"F7.wireOp",EDGE,"E31");var subQ4=makeQuery(id+"F7.imprint","INTERSECT",VERTEX,{"disambiguationData":[OD(1.0)],"derivedFrom":[subQ1,subQ3]});Q10=makeQuery(id+"F7.imprint","IMPRINT",FACE,{"disambiguationData":[TD([[makeQuery(id+"F7.imprint","IMPRINT",EDGE,{"disambiguationData":[TD([[subQ4,1.0]])],"derivedFrom":subQ3}),1.0]])]});}
            var Q11;
            {var subQ1=sQuery(id+"F7.wireOp",EDGE,"E27");var subQ3=sQuery(id+"F7.wireOp",EDGE,"E31");var subQ4=makeQuery(id+"F7.imprint","INTERSECT",VERTEX,{"disambiguationData":[OD(1.0)],"derivedFrom":[subQ1,subQ3]});Q11=makeQuery(id+"F7.imprint","IMPRINT",FACE,{"disambiguationData":[TD([[makeQuery(id+"F7.imprint","IMPRINT",EDGE,{"disambiguationData":[TD([[subQ4,-1.0]])],"derivedFrom":subQ3}),1.0]])]});}
            extrude(context, id + "F13", {"entities" : qUnion([Q0, Q1, Q2, Q3, Q4, Q5, Q6, Q7, Q8, Q9, Q10, Q11]), "operationType" : NewBodyOperationType.REMOVE, "oppositeDirection" : true, "depth" : 0.5 * mm, "offsetDistance" : 25 * mm});
        }
        {
            var Q0;
            {var subQ1=sQuery(id+"F6.wireOp",EDGE,"E22");var subQ3=sQuery(id+"F6.wireOp",EDGE,"E25");var subQ4=makeQuery(id+"F6.imprint","INTERSECT",VERTEX,{"disambiguationData":[OD(1.0)],"derivedFrom":[subQ1,subQ3]});Q0=makeQuery(id+"F6.imprint","IMPRINT",FACE,{"disambiguationData":[TD([[makeQuery(id+"F6.imprint","IMPRINT",EDGE,{"disambiguationData":[TD([[subQ4,1.0]])],"derivedFrom":subQ3}),1.0]])]});}
            var Q1;
            {var subQ1=sQuery(id+"F6.wireOp",EDGE,"E22");var subQ3=sQuery(id+"F6.wireOp",EDGE,"E25");var subQ4=makeQuery(id+"F6.imprint","INTERSECT",VERTEX,{"disambiguationData":[OD(1.0)],"derivedFrom":[subQ1,subQ3]});Q1=makeQuery(id+"F6.imprint","IMPRINT",FACE,{"disambiguationData":[TD([[makeQuery(id+"F6.imprint","IMPRINT",EDGE,{"disambiguationData":[TD([[subQ4,-1.0]])],"derivedFrom":subQ3}),1.0]])]});}
            var Q2;
            {var subQ1=sQuery(id+"F6.wireOp",EDGE,"E22");var subQ3=sQuery(id+"F6.wireOp",EDGE,"E25");var subQ4=makeQuery(id+"F6.imprint","INTERSECT",VERTEX,{"disambiguationData":[OD(0.0)],"derivedFrom":[subQ1,subQ3]});Q2=makeQuery(id+"F6.imprint","IMPRINT",FACE,{"disambiguationData":[TD([[makeQuery(id+"F6.imprint","IMPRINT",EDGE,{"disambiguationData":[TD([[subQ4,-1.0]])],"derivedFrom":subQ3}),1.0]])]});}
            var Q3;
            {var subQ1=sQuery(id+"F6.wireOp",EDGE,"E22");var subQ3=sQuery(id+"F6.wireOp",EDGE,"E25");var subQ4=makeQuery(id+"F6.imprint","INTERSECT",VERTEX,{"disambiguationData":[OD(0.0)],"derivedFrom":[subQ1,subQ3]});Q3=makeQuery(id+"F6.imprint","IMPRINT",FACE,{"disambiguationData":[TD([[makeQuery(id+"F6.imprint","IMPRINT",EDGE,{"disambiguationData":[TD([[subQ4,1.0]])],"derivedFrom":subQ3}),1.0]])]});}
            var Q4;
            {var subQ1=sQuery(id+"F6.wireOp",EDGE,"E22");var subQ3=sQuery(id+"F6.wireOp",EDGE,"E26");var subQ4=makeQuery(id+"F6.imprint","INTERSECT",VERTEX,{"disambiguationData":[OD(1.0)],"derivedFrom":[subQ1,subQ3]});Q4=makeQuery(id+"F6.imprint","IMPRINT",FACE,{"disambiguationData":[TD([[makeQuery(id+"F6.imprint","IMPRINT",EDGE,{"disambiguationData":[TD([[subQ4,1.0]])],"derivedFrom":subQ3}),1.0]])]});}
            var Q5;
            {var subQ1=sQuery(id+"F6.wireOp",EDGE,"E22");var subQ3=sQuery(id+"F6.wireOp",EDGE,"E26");var subQ4=makeQuery(id+"F6.imprint","INTERSECT",VERTEX,{"disambiguationData":[OD(1.0)],"derivedFrom":[subQ1,subQ3]});Q5=makeQuery(id+"F6.imprint","IMPRINT",FACE,{"disambiguationData":[TD([[makeQuery(id+"F6.imprint","IMPRINT",EDGE,{"disambiguationData":[TD([[subQ4,-1.0]])],"derivedFrom":subQ3}),1.0]])]});}
            var Q6;
            {var subQ1=sQuery(id+"F6.wireOp",EDGE,"E22");var subQ3=sQuery(id+"F6.wireOp",EDGE,"E26");var subQ4=makeQuery(id+"F6.imprint","INTERSECT",VERTEX,{"disambiguationData":[OD(0.0)],"derivedFrom":[subQ1,subQ3]});Q6=makeQuery(id+"F6.imprint","IMPRINT",FACE,{"disambiguationData":[TD([[makeQuery(id+"F6.imprint","IMPRINT",EDGE,{"disambiguationData":[TD([[subQ4,-1.0]])],"derivedFrom":subQ3}),1.0]])]});}
            var Q7;
            {var subQ1=sQuery(id+"F6.wireOp",EDGE,"E22");var subQ3=sQuery(id+"F6.wireOp",EDGE,"E26");var subQ4=makeQuery(id+"F6.imprint","INTERSECT",VERTEX,{"disambiguationData":[OD(0.0)],"derivedFrom":[subQ1,subQ3]});Q7=makeQuery(id+"F6.imprint","IMPRINT",FACE,{"disambiguationData":[TD([[makeQuery(id+"F6.imprint","IMPRINT",EDGE,{"disambiguationData":[TD([[subQ4,1.0]])],"derivedFrom":subQ3}),1.0]])]});}
            extrude(context, id + "F14", {"entities" : qUnion([Q0, Q1, Q2, Q3, Q4, Q5, Q6, Q7]), "operationType" : NewBodyOperationType.REMOVE, "oppositeDirection" : true, "depth" : 0.5 * mm, "offsetDistance" : 25 * mm});
        }
    });
